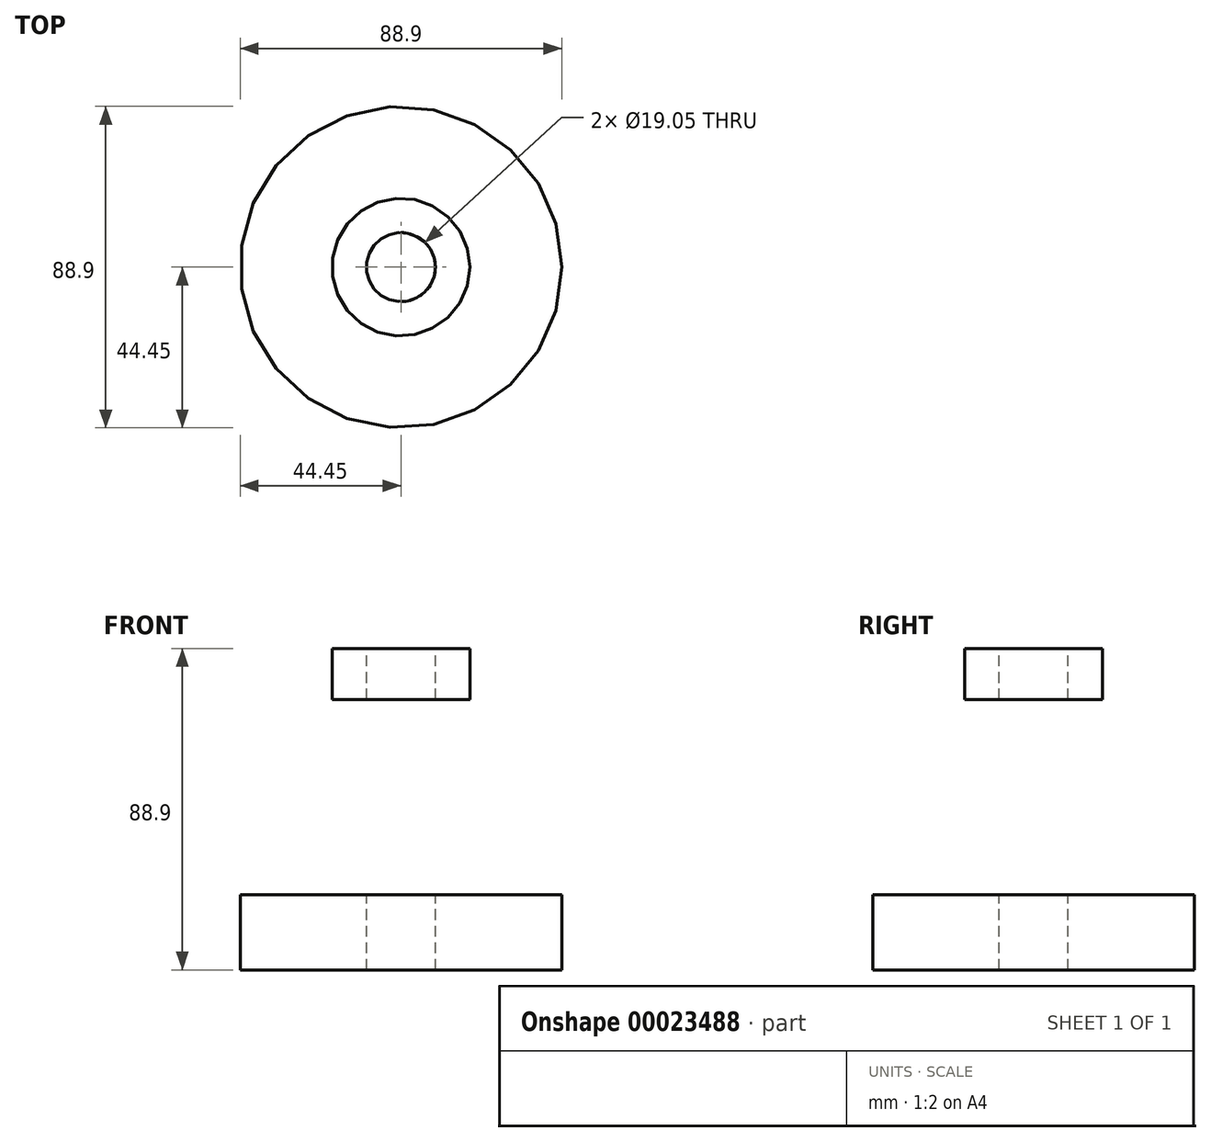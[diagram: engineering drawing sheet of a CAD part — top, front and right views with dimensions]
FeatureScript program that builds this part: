
annotation { "Feature Type Name" : "Feature", "Feature Type Description" : "" }
export const myFeature = defineFeature(function(context is Context, id is Id, definition is map)
    precondition{}
    {
        {
            var Q0;
            Q0=qCreatedBy(makeId("Front.planeOp"),FACE);
            var sketch = newSketch(context, id + "F0", { "sketchPlane" : qUnion([Q0])});
            skLineSegment(sketch, "E0", {"start": v(0, 51.32) * mm, "end": v(0, -37.58) * mm, "construction": true});
            skLineSegment(sketch, "E1.left", {"start": v(0, 51.32) * mm, "end": v(0, 51.32) * mm});
            skLineSegment(sketch, "E2", {"start": v(9.53, 51.32) * mm, "end": v(9.52, -37.58) * mm});
            skLineSegment(sketch, "E3.bottom", {"start": v(9.53, 51.32) * mm, "end": v(19.05, 51.32) * mm});
            skLineSegment(sketch, "E3.top", {"start": v(9.53, 37.2) * mm, "end": v(19.05, 37.2) * mm});
            skLineSegment(sketch, "E3.left", {"start": v(9.53, 51.32) * mm, "end": v(9.53, 37.2) * mm});
            skLineSegment(sketch, "E3.right", {"start": v(19.05, 51.32) * mm, "end": v(19.05, 37.2) * mm});
            skLineSegment(sketch, "E4.bottom", {"start": v(9.53, 37.2) * mm, "end": v(25.4, 37.2) * mm});
            skLineSegment(sketch, "E4.top", {"start": v(9.53, -16.82) * mm, "end": v(25.4, -16.82) * mm});
            skLineSegment(sketch, "E4.left", {"start": v(9.53, 37.2) * mm, "end": v(9.53, -16.82) * mm});
            skLineSegment(sketch, "E4.right", {"start": v(25.4, 37.2) * mm, "end": v(25.4, -16.82) * mm});
            skLineSegment(sketch, "E5.bottom", {"start": v(9.52, -37.58) * mm, "end": v(44.45, -37.58) * mm});
            skLineSegment(sketch, "E5.top", {"start": v(9.52, -16.82) * mm, "end": v(44.45, -16.82) * mm});
            skLineSegment(sketch, "E5.left", {"start": v(9.52, -37.58) * mm, "end": v(9.52, -16.82) * mm});
            skLineSegment(sketch, "E5.right", {"start": v(44.45, -37.58) * mm, "end": v(44.45, -16.82) * mm});
            skSolve(sketch);
        }
        {
            var Q0;
            {var subQ2=sQuery(id+"F0.wireOp",EDGE,"E4.left");Q0=makeQuery(id+"F0.imprint","IMPRINT",FACE,{"disambiguationData":[TD([[makeQuery(id+"F0.imprint","IMPRINT",EDGE,{"derivedFrom":subQ2}),1.0]])]});}
            var Q1;
            Q1=makeQuery(id+"F0.imprint","IMPRINT",FACE,{"disambiguationData":[TD([[makeQuery(id+"F0.imprint","IMPRINT",EDGE,{"derivedFrom":sQuery(id+"F0.wireOp",EDGE,"E5.bottom")}),1.0]])]});
            var Q2;
            Q2=makeQuery(id+"F0.imprint","IMPRINT",FACE,{"disambiguationData":[TD([[makeQuery(id+"F0.imprint","IMPRINT",EDGE,{"derivedFrom":sQuery(id+"F0.wireOp",EDGE,"E3.bottom")}),-1.0]])]});
            var Q3;
            Q3=sQuery(id+"F0.wireOp",EDGE,"E0");
            revolve(context, id + "F1", {"entities" : qUnion([Q0, Q1, Q2]), "axis" : qUnion([Q3]), "revolveType" : RevolveType.FULL});
        }
    });
